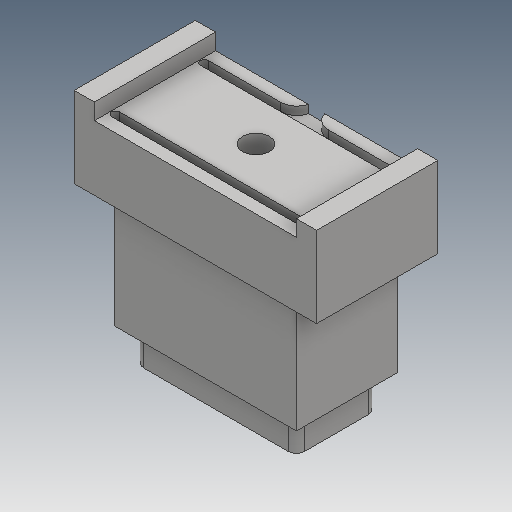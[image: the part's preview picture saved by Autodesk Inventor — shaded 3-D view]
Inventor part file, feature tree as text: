
AUTODESK INVENTOR PART (.ipt)
format: ipt  version: 2019 (Build 230136000, 136)  size: 243,712 bytes
history: native  units: mm
features: sketch x8, extrude x6, projected_geometry x6, fillet x3, hole x2
ambient origin geometry x8: Origin, YZ Plane, XZ Plane, XY Plane, X Axis, Y Axis, Z Axis, Center Point
bodies: Solid1 (feature_tree)
feature tree (25):
  extrude  "Extrusion1"  Depth=30.0mm
  extrude  "Extrusion2"  Depth=10.0mm TaperAngle=0.0deg
  extrude  "Extrusion3"  Depth=2.0mm
  extrude  "Extrusion4"  Depth=19.9mm
  hole  "Hole1"  [1 undecoded]
  fillet  "Fillet1"  Radius=1.0mm
  hole  "Hole3"  [1 undecoded]
  extrude  "Extrusion5"  Depth=2.0mm
  fillet  "Fillet2"  Radius=0.625mm
  extrude  "Extrusion6"  Depth=2.0mm
  fillet  "Fillet3"  Radius=0.625mm
  sketch  "Sketch1"  dims[d0=15.0mm d1=30.0mm]
  sketch  "Sketch2"  dims[d2=10.0mm d3=0.0mm d5=14.0mm d6=0.0mm]
  projected_geometry  "Projected Loop1"
  sketch  "Sketch3"  dims[d7=2.0mm d8=25.0mm]
  projected_geometry  "Projected Loop2"
  sketch  "Sketch4"  dims[d9=15.0mm d10=0.0mm d11=19.9mm]
  projected_geometry  "Projected Loop3"
  sketch  "Sketch5"  dims[d12=9.9mm d13=4.0mm d14=0.0mm]
  sketch  "Sketch7"  dims[d15=3.3mm d16=6.0mm d17=4.0mm d18=2.0mm d19=90.0deg d20=8.0mm d21=20.594885mm d22=1.0mm]
  projected_geometry  "Projected Loop6"
  sketch  "Sketch8"  dims[d32=12.5mm d33=22.5mm]
  projected_geometry  "Projected Loop7"
  sketch  "Sketch9"  dims[d34=0.625mm d35=5.5mm d36=0.625mm d37=5.5mm d38=0.625mm d39=0.625mm d40=5.5mm d41=5.5mm d42=1.0mm d43=6.0mm d44=4.0mm d45=2.0mm d46=90.0deg d47=8.0mm d48=20.594885mm d49=1.0mm d50=0.625mm d51=0.999952mm d52=0.625mm d53=1.0mm d54=0.0mm d55=2.0mm d56=2.0mm d57=1.0mm d58=0.0mm d59=2.0mm]
  projected_geometry  "Projected Loop8"
note: 2 required parameter values undecoded (feature->parameter linkage not recoverable at this tier; creation-order binding heuristic only, values carry confidence <= 0.55)
